# Revit family: PGR
name_source: partatom
category: Lighting Fixtures
revit_build: Autodesk Revit Architecture 2012 (Build: 20110309_2315(x64)
units: mm (PartAtom-declared; Revit-internal decimal feet)

## types (4) — shared parameters
Color Filter = 16777215
Default Elevation = 48 "
Description = Indoor or Outdoor High Performance LED Remote
Dimming Lamp Color Temperature Shift = <None>
Emit Shape Visible in Rendering = No
Emit from Rectangle Length = 1 "
Emit from Rectangle Width = 6 "
Lamp = LED
Lens = Hubbell - White Glass
Load Classification = Lighting
Manufacturer = Dual Lite
Manufacturer Fax = (866)-898-0131
Model = PGR
Photometric Web File = pgrseries.ies
Product Documentation Link = http://cdn.dual-lite.com
Product Page URL = http://www.dual-lite.com
Tilt Angle = 90.00°
Total Input Wattage = 12 & 13W
URL = http://www.dual-lite.com
Voltage = 120 V

## per-type parameters (varying)
| type | Apparent Load | Finish |
| PGR - Dark Bronze | 13 VA | Hubbell-Aluminum-Dark Bronze |
| PGR - Black | 12 VA | Hubbell-Aluminum- Black |
| PGR - White | 12 VA | Hubbell-Aluminum- White |
| PGR - Platinum Silver | 12 VA | Hubbell - Aluminium- Platinum Silver |

## geometry (parser evidence)
native form markers: Blend x10, Sweep x5
no freeform markers — native parametric forms only
